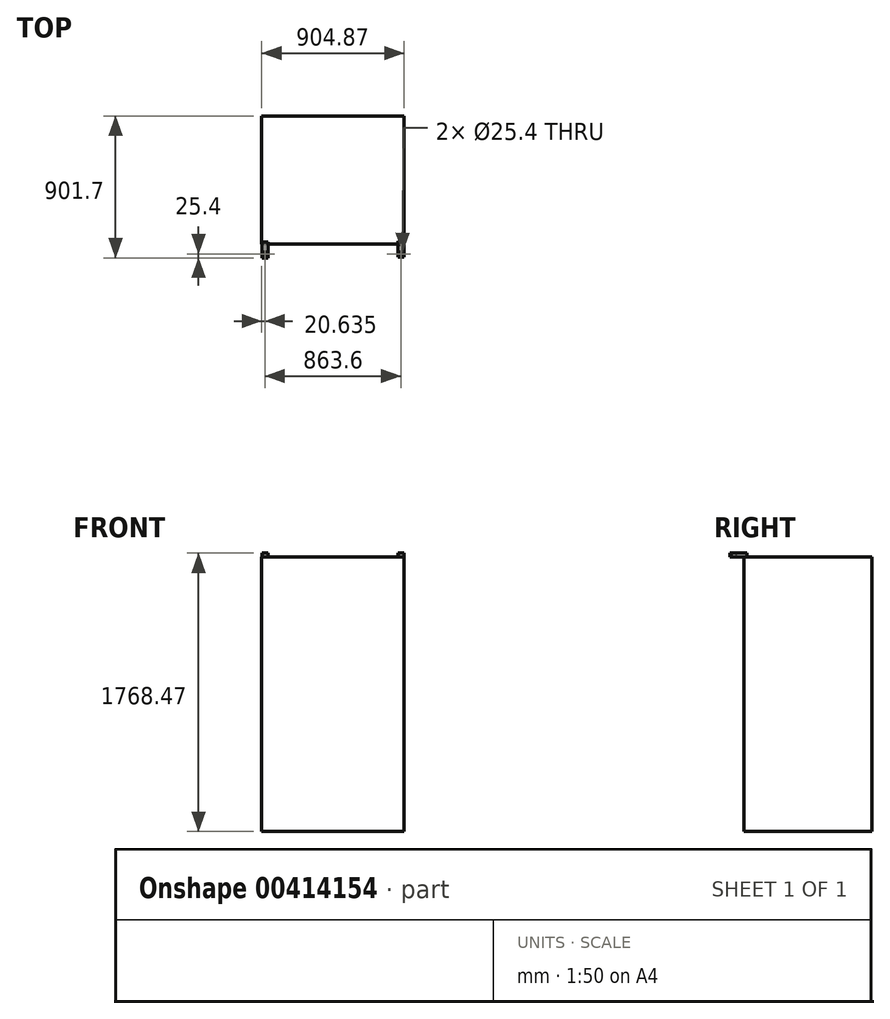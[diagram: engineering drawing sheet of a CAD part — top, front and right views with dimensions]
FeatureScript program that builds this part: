
annotation { "Feature Type Name" : "Feature", "Feature Type Description" : "" }
export const myFeature = defineFeature(function(context is Context, id is Id, definition is map)
    precondition{}
    {
        {
            var Q0;
            Q0=qCreatedBy(makeId("Front.planeOp"),FACE);
            var sketch = newSketch(context, id + "F0", { "sketchPlane" : qUnion([Q0])});
            skLineSegment(sketch, "E0.bottom", {"start": v(-454.1, -703.1) * mm, "end": v(450.77, -703.1) * mm});
            skLineSegment(sketch, "E0.top", {"start": v(-454.1, 1039.98) * mm, "end": v(450.77, 1039.98) * mm});
            skLineSegment(sketch, "E0.left", {"start": v(-454.1, -703.1) * mm, "end": v(-454.1, 1039.98) * mm});
            skLineSegment(sketch, "E0.right", {"start": v(450.77, -703.1) * mm, "end": v(450.77, 1039.98) * mm});
            skSolve(sketch);
        }
        {
            var Q0;
            Q0=makeQuery(id+"F0.imprint","IMPRINT",FACE,{"disambiguationData":[TD([[makeQuery(id+"F0.imprint","IMPRINT",EDGE,{"derivedFrom":sQuery(id+"F0.wireOp",EDGE,"E0.bottom")}),1.0]])]});
            extrude(context, id + "F1", {"entities" : qUnion([Q0]), "depth" : 812.8 * mm});
        }
        {
            var Q0;
            Q0=makeQuery(id+"F1.opExtrude","SWEPT_FACE",FACE,{"disambiguationData":[OSD([sQuery(id+"F0.wireOp",EDGE,"E0.top")])]});
            var sketch = newSketch(context, id + "F2", { "sketchPlane" : qUnion([Q0])});
            skLineSegment(sketch, "E1.bottom", {"start": v(-452.51, -800.1) * mm, "end": v(-414.41, -800.1) * mm});
            skLineSegment(sketch, "E1.top", {"start": v(-452.51, -901.7) * mm, "end": v(-414.41, -901.7) * mm});
            skLineSegment(sketch, "E1.left", {"start": v(-452.51, -800.1) * mm, "end": v(-452.51, -901.7) * mm});
            skLineSegment(sketch, "E1.right", {"start": v(-414.41, -800.1) * mm, "end": v(-414.41, -901.7) * mm});
            skCircle(sketch, "E2", {"center": v(-433.46, -876.3) * mm, "radius": 12.7 * mm});
            skLineSegment(sketch, "E3.bottom", {"start": v(411.09, -793.75) * mm, "end": v(449.19, -793.75) * mm});
            skLineSegment(sketch, "E3.top", {"start": v(411.09, -895.35) * mm, "end": v(449.19, -895.35) * mm});
            skLineSegment(sketch, "E3.left", {"start": v(411.09, -793.75) * mm, "end": v(411.09, -895.35) * mm});
            skLineSegment(sketch, "E3.right", {"start": v(449.19, -793.75) * mm, "end": v(449.19, -895.35) * mm});
            skCircle(sketch, "E4", {"center": v(430.14, -876.3) * mm, "radius": 12.7 * mm});
            skPoint(sketch, "E4.centerSnap0", {"position": v(430.14, -895.35) * mm});
            skSolve(sketch);
        }
        {
            var Q0;
            Q0 = qSketchRegion(id + "F2", true);
            extrude(context, id + "F3", {"entities" : qUnion([Q0]), "operationType" : NewBodyOperationType.ADD, "depth" : 25.4 * mm});
        }
    });
